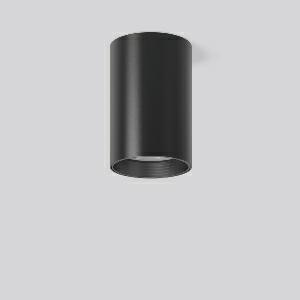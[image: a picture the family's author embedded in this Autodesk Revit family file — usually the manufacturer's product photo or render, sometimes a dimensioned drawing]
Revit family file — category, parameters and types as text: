
# Revit family: heledon_maxi_a_931221_003_2_76_55e6
name_source: partatom
category: Lighting Fixtures
units: mm (PartAtom-declared; Revit-internal decimal feet)

## family parameters
Cut with Voids When Loaded = No
Host = Face
Light Source = No
Part Type = Normal
Room Calculation Point = No
Round Connector Dimension = Use Diameter
Shared = No

## types (1)
- HELEDON maxi A (1 x LED Modul 927, 2550 lm, 2700)
    Apparent Load = 25 VA
    Approval mark = CE
    CIE Flux Codes = 96 100 100 100 100
    Color Rendering = 92
    Color Temperature = 2700
    Default Elevation = 1800 mm
    Description = Series: HELEDON maxi
Cylindrical surface-mounted downlight. Housing: die-cast aluminium, powder-coated. Internal ceiling frame polycarbonate with bayonet mounting. Black plastic ring and recessed LED to prevent glare from the side. Optical assembly with lens made of plastic (polycarbonate) for the best homogeneous light distribution - can be changed without tools. Best colour rendering index Ra>90. Suitable for Ceiling mounting. Easy installation with a separate ceiling frame with bayonet mounting and plug connection. Driver integrated. Connected via plug-in connector. High quality converter without flickering and stroboscopic effect. The following accessories can be mounted without use of tools: interchangeable lenses, decorative glasses, honeycomb louvre, clear and frosted diffusers, white interchangeable plastic ring. 
Colour: deep black, matt (RAL 9005)
Diameter: 123 mm
Height: 183 mm
Lamp: LED
Socket: without socket
Colour temperature: 2700K
Colour rendering index (CRI): 92
System power: 25 W
Rated luminous flux: 2550 lm
Luminous efficiency: 102 lm/W
Control gear: Converter, dimmable, DALI
Protection class: I
Type of protection: IP 20
    Height = 183 mm
    Lamp = 1 x LED Modul 927
    Lamp Light Flux = 2550 lm
    Lamp count = 1
    Length = 123 mm
    Lifetime = 50000 h
    Luminous efficacy = 102 lm/W
    Manufacturer = RZB
    ModVariant = No
    Model = 931221.003.2.76
    Mounting Place = Ceiling
    Mounting Type = Surface mounted
    Number of Poles = 1
    OnlyDefault = Yes
    Power Factor = 1
    Product Name = HELEDON maxi A
    Product group = Surface mounted downlights
    ProductGroupID = 302
    Protection Class = Protection class I
    Protection Degree = IP 20
    RLX_Detail_Level = 1
    RLX_Emergency_Light_Flux = 0 lm
    RLX_Emergency_Type = 0
    RLX_Emergency_Type_DB = No
    RlxData = <blob elided: 97009 chars, md5=4cf0060b>
    Socket = socket
    Standby Power = 0 W
    System Light Flux = 2550 lm
    System Power = 25 W
    Type Comments = Product without accessories
    Type Image = 931193.003.jpg
    URL = http://relux.com
    VarID = ---
    Voltage = 230 V
    Voltage Range = 220-240 V
    Weight = 0.00 kg
    Width = 0 mm  [stored 0 ft]

note: [stored X ft] marks values corroborated as IEEE doubles in the binary element streams (Revit-internal decimal feet)

## geometry (parser evidence)
native form markers: Blend x4, Sweep x9
no freeform markers — native parametric forms only
